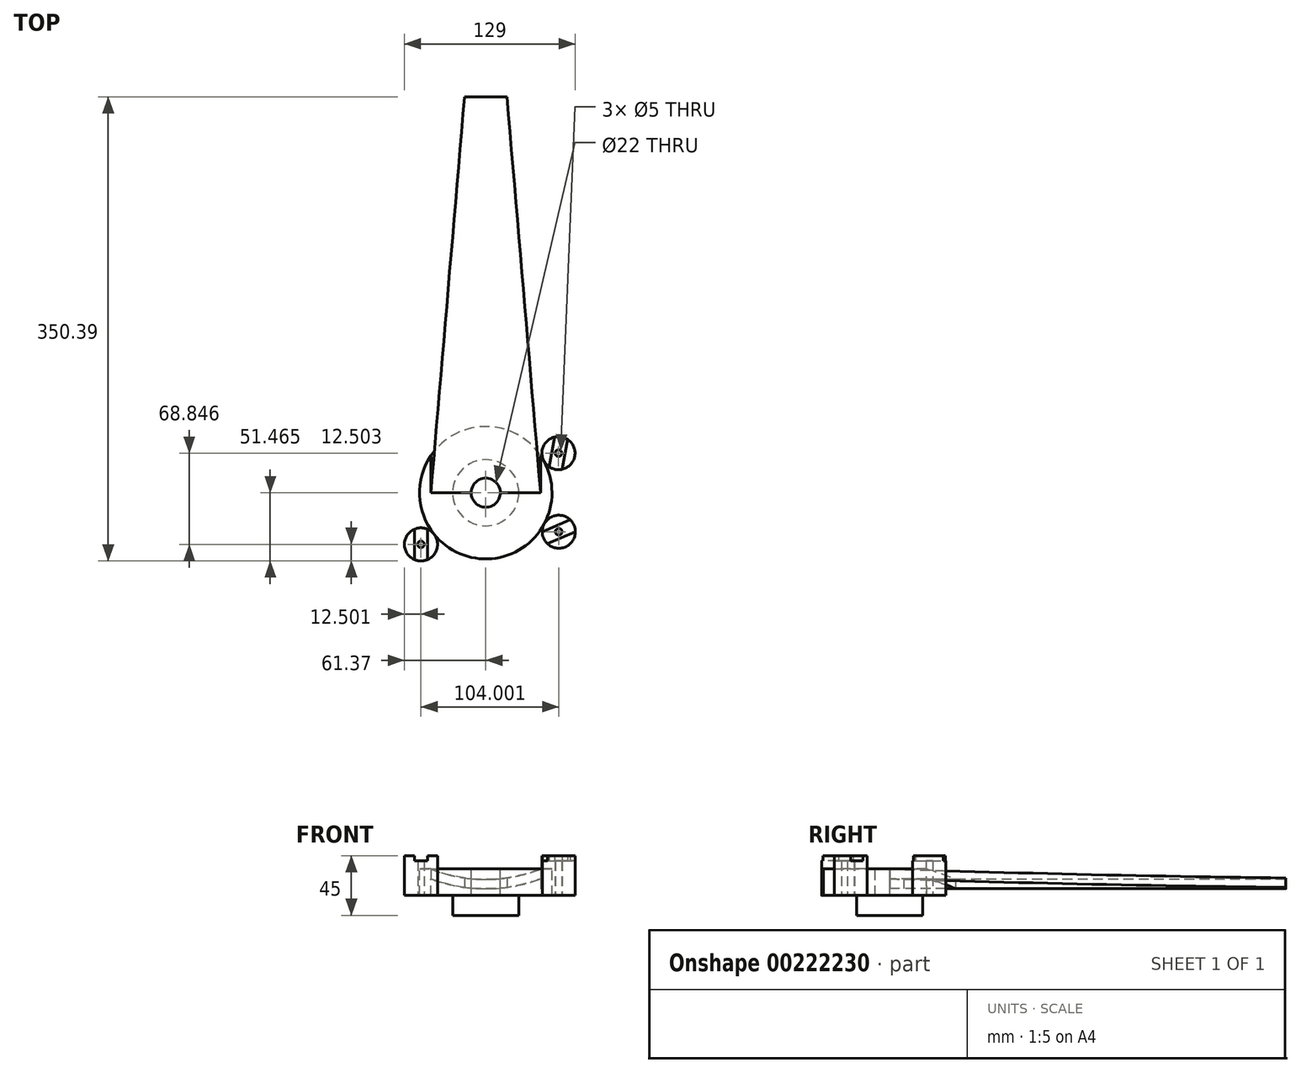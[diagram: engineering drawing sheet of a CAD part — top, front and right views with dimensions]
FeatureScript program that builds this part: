
annotation { "Feature Type Name" : "Feature", "Feature Type Description" : "" }
export const myFeature = defineFeature(function(context is Context, id is Id, definition is map)
    precondition{}
    {
        {
            var Q0;
            Q0=qCreatedBy(makeId("Top.planeOp"),FACE);
            var sketch = newSketch(context, id + "F0", { "sketchPlane" : qUnion([Q0])});
            skLineSegment(sketch, "E0", {"start": v(-16, 139.35) * mm, "end": v(-41.41, -159.57) * mm});
            skLineSegment(sketch, "E1", {"start": v(0, -151.5) * mm, "end": v(0, 130.37) * mm});
            skLineSegment(sketch, "E2.MirrorCS", {"start": v(16, 139.35) * mm, "end": v(41.41, -159.57) * mm});
            skLineSegment(sketch, "E3", {"start": v(-16, 139.35) * mm, "end": v(16, 139.35) * mm});
            skLineSegment(sketch, "E4", {"start": v(-41.41, -159.57) * mm, "end": v(41.41, -159.57) * mm});
            skSolve(sketch);
        }
        {
            var Q0;
            Q0=makeQuery(id+"F0.imprint","IMPRINT",FACE,{"disambiguationData":[TD([[makeQuery(id+"F0.imprint","IMPRINT",EDGE,{"derivedFrom":sQuery(id+"F0.wireOp",EDGE,"E0")}),1.0]])]});
            extrude(context, id + "F12", {"entities" : qUnion([Q0]), "depth" : 20 * mm});
        }
        {
            var Q0;
            Q0=makeQuery(id+"F12.opExtrude","CAP_FACE",FACE,{"disambiguationData":[OSD([sQuery(id+"F0.wireOp",EDGE,"E0"),sQuery(id+"F0.wireOp",EDGE,"E2.MirrorCS"),sQuery(id+"F0.wireOp",EDGE,"E3"),sQuery(id+"F0.wireOp",EDGE,"E4")])],"isStart":false});
            var sketch = newSketch(context, id + "F13", { "sketchPlane" : qUnion([Q0])});
            skCircle(sketch, "E5", {"center": v(0, -159.57) * mm, "radius": 50 * mm});
            skSolve(sketch);
        }
        {
            var Q0;
            {var subQ5=makeQuery(id+"F12.opExtrude","CAP_EDGE",EDGE,{"disambiguationData":[OSD([sQuery(id+"F0.wireOp",EDGE,"E4")])],"isStart":false});Q0=makeQuery(id+"F13.imprint","IMPRINT",FACE,{"disambiguationData":[TD([[makeQuery(id+"F13.imprint","IMPRINT",EDGE,{"derivedFrom":subQ5}),-1.0]])]});}
            var Q1;
            {var subQ5=makeQuery(id+"F12.opExtrude","CAP_EDGE",EDGE,{"disambiguationData":[OSD([sQuery(id+"F0.wireOp",EDGE,"E4")])],"isStart":false});Q1=makeQuery(id+"F13.imprint","IMPRINT",FACE,{"disambiguationData":[TD([[makeQuery(id+"F13.imprint","IMPRINT",EDGE,{"derivedFrom":subQ5}),1.0]])]});}
            extrude(context, id + "F1", {"entities" : qUnion([Q0, Q1]), "oppositeDirection" : true, "depth" : 20 * mm});
        }
        {
            var Q0;
            Q0=makeQuery(id+"F12.opExtrude","SWEPT_FACE",FACE,{"disambiguationData":[OSD([sQuery(id+"F0.wireOp",EDGE,"E4")])]});
            var sketch = newSketch(context, id + "F2", { "sketchPlane" : qUnion([Q0])});
            skArc(sketch, "E6", {"start": v(-41.41, 20) * mm, "mid": v(0, 12.05) * mm, "end": v(41.41, 20) * mm});
            skSolve(sketch);
        }
        {
            var Q0;
            Q0=makeQuery(id+"F2.imprint","IMPRINT",FACE,{"disambiguationData":[TD([[makeQuery(id+"F2.imprint","IMPRINT",EDGE,{"derivedFrom":sQuery(id+"F2.wireOp",EDGE,"E6")}),1.0]])]});
            extrude(context, id + "F14", {"entities" : qUnion([Q0]), "operationType" : NewBodyOperationType.REMOVE, "endBound" : BoundingType.THROUGH_ALL, "oppositeDirection" : true, "depth" : 25 * mm});
        }
        {
            var Q0;
            Q0=makeQuery(id+"F2.imprint","IMPRINT",FACE,{"disambiguationData":[TD([[makeQuery(id+"F2.imprint","IMPRINT",EDGE,{"derivedFrom":sQuery(id+"F2.wireOp",EDGE,"E6")}),-1.0]])]});
            var sketch = newSketch(context, id + "F3", { "sketchPlane" : qUnion([Q0])});
            skArc(sketch, "E7.0", {"start": v(-41.41, 20) * mm, "mid": v(0, 12.05) * mm, "end": v(41.41, 20) * mm});
            skArc(sketch, "E8.0", {"start": v(-44, 13.5) * mm, "mid": v(0, 5.05) * mm, "end": v(44, 13.5) * mm});
            skSolve(sketch);
        }
        {
            var Q0;
            Q0=makeQuery(id+"F2.imprint","IMPRINT",FACE,{"disambiguationData":[TD([[makeQuery(id+"F2.imprint","IMPRINT",EDGE,{"derivedFrom":sQuery(id+"F2.wireOp",EDGE,"E6")}),-1.0]])]});
            var sketch = newSketch(context, id + "F15", { "sketchPlane" : qUnion([Q0])});
            skLineSegment(sketch, "E9.0", {"start": v(-41.41, 20) * mm, "end": v(-41.41, 0) * mm});
            skLineSegment(sketch, "E10.0", {"start": v(-41.41, 0) * mm, "end": v(41.41, 0) * mm});
            skLineSegment(sketch, "E11.0", {"start": v(41.41, 20) * mm, "end": v(41.41, 0) * mm});
            skSolve(sketch);
        }
        {
            var Q0;
            Q0=qSketchRegion(id+"F15",true);
            var Q1;
            {var subQ1=sQuery(id+"F0.wireOp",EDGE,"E4");var subQ6=makeQuery(id+"F2.imprint","IMPRINT",EDGE,{"derivedFrom":makeQuery(id+"F12.opExtrude","CAP_EDGE",EDGE,{"disambiguationData":[OSD([subQ1])],"isStart":true})});Q1=makeQuery(id+"F3.imprint","IMPRINT",FACE,{"disambiguationData":[TD([[makeQuery(id+"F3.imprint","IMPRINT",EDGE,{"derivedFrom":subQ6}),1.0]])]});}
            extrude(context, id + "F4", {"entities" : qUnion([Q0, Q1]), "operationType" : NewBodyOperationType.REMOVE, "endBound" : BoundingType.THROUGH_ALL, "oppositeDirection" : true, "depth" : 25 * mm});
        }
        {
            var Q0;
            Q0=makeQuery(id+"F1.opExtrude","CAP_FACE",FACE,{"disambiguationData":[OSD([sQuery(id+"F13.wireOp",EDGE,"E5")])],"isStart":true});
            var sketch = newSketch(context, id + "F5", { "sketchPlane" : qUnion([Q0])});
            skCircle(sketch, "E12.0", {"center": v(0, -159.57) * mm, "radius": 50 * mm});
            skCircle(sketch, "E13", {"center": v(0, -159.57) * mm, "radius": 11 * mm});
            skSolve(sketch);
        }
        {
            var Q0;
            Q0=makeQuery(id+"F5.imprint","IMPRINT",FACE,{"disambiguationData":[TD([[makeQuery(id+"F5.imprint","IMPRINT",EDGE,{"derivedFrom":sQuery(id+"F5.wireOp",EDGE,"E13")}),1.0]])]});
            extrude(context, id + "F16", {"entities" : qUnion([Q0]), "operationType" : NewBodyOperationType.REMOVE, "endBound" : BoundingType.THROUGH_ALL, "oppositeDirection" : true, "depth" : 25 * mm});
        }
        {
            var Q0;
            Q0=makeQuery(id+"F1.opExtrude","CAP_FACE",FACE,{"disambiguationData":[OSD([sQuery(id+"F13.wireOp",EDGE,"E5")])],"isStart":true});
            var sketch = newSketch(context, id + "F6", { "sketchPlane" : qUnion([Q0])});
            skCircle(sketch, "E14.0", {"center": v(0, -159.57) * mm, "radius": 11 * mm});
            skSolve(sketch);
        }
        {
            var Q0;
            Q0=makeQuery(id+"F6.imprint","IMPRINT",FACE,{"disambiguationData":[TD([[makeQuery(id+"F6.imprint","IMPRINT",EDGE,{"derivedFrom":sQuery(id+"F6.wireOp",EDGE,"E14.0")}),1.0]])]});
            extrude(context, id + "F17", {"entities" : qUnion([Q0]), "operationType" : NewBodyOperationType.REMOVE, "endBound" : BoundingType.THROUGH_ALL, "oppositeDirection" : true, "depth" : 25 * mm});
        }
        {
            var Q0;
            Q0=makeQuery(id+"F1.opExtrude","CAP_FACE",FACE,{"disambiguationData":[OSD([sQuery(id+"F13.wireOp",EDGE,"E5")])],"isStart":false});
            var sketch = newSketch(context, id + "F18", { "sketchPlane" : qUnion([Q0])});
            skCircle(sketch, "E15", {"center": v(-48.87, 198.54) * mm, "radius": 12.5 * mm});
            skCircle(sketch, "E16", {"center": v(-48.87, 198.54) * mm, "radius": 2.5 * mm});
            skSolve(sketch);
        }
        {
            var Q0;
            Q0=makeQuery(id+"F18.imprint","IMPRINT",FACE,{"disambiguationData":[TD([[makeQuery(id+"F18.imprint","IMPRINT",EDGE,{"derivedFrom":sQuery(id+"F18.wireOp",EDGE,"E15")}),1.0]])]});
            extrude(context, id + "F7", {"entities" : qUnion([Q0]), "oppositeDirection" : true, "depth" : 30 * mm});
        }
        {
            var Q0;
            Q0=makeQuery(id+"F7.opExtrude","CAP_FACE",FACE,{"disambiguationData":[OSD([sQuery(id+"F18.wireOp",EDGE,"E15"),sQuery(id+"F18.wireOp",EDGE,"E16")])],"isStart":false});
            var sketch = newSketch(context, id + "F19", { "sketchPlane" : qUnion([Q0])});
            skLineSegment(sketch, "E17.bottom", {"start": v(-43.87, -180.65) * mm, "end": v(-53.87, -180.65) * mm});
            skLineSegment(sketch, "E17.top", {"start": v(-43.87, -212.63) * mm, "end": v(-53.87, -212.63) * mm});
            skLineSegment(sketch, "E17.left", {"start": v(-43.87, -180.65) * mm, "end": v(-43.87, -212.63) * mm});
            skLineSegment(sketch, "E17.right", {"start": v(-53.87, -180.65) * mm, "end": v(-53.87, -212.63) * mm});
            skCircle(sketch, "E18.0", {"center": v(-48.87, -198.54) * mm, "radius": 2.5 * mm});
            skSolve(sketch);
        }
        {
            var Q0;
            Q0=qSketchRegion(id+"F19",true);
            var Q1;
            Q1=makeQuery(id+"F19.imprint","IMPRINT",FACE,{"disambiguationData":[TD([[makeQuery(id+"F19.imprint","IMPRINT",EDGE,{"derivedFrom":sQuery(id+"F19.wireOp",EDGE,"E18.0")}),1.0]])]});
            extrude(context, id + "F8", {"entities" : qUnion([Q0, Q1]), "operationType" : NewBodyOperationType.REMOVE, "oppositeDirection" : true, "depth" : 4 * mm});
        }
        {
            var Q0;
            Q0=makeQuery(id+"F15.imprint","IMPRINT",FACE,{"disambiguationData":[TD([[makeQuery(id+"F15.imprint","IMPRINT",EDGE,{"derivedFrom":sQuery(id+"F15.wireOp",EDGE,"E9.0")}),1.0]])]});
            var sketch = newSketch(context, id + "F9", { "sketchPlane" : qUnion([Q0])});
            skLineSegment(sketch, "E19", {"start": v(0, 0) * mm, "end": v(0, 7.48) * mm});
            skSolve(sketch);
        }
        {
            var Q0;
            Q0=makeQuery(id+"F7.opExtrude","SWEPT_BODY",BODY,{"disambiguationData":[OSD([sQuery(id+"F18.wireOp",EDGE,"E15"),sQuery(id+"F18.wireOp",EDGE,"E16")])]});
            var Q1;
            Q1=sQuery(id+"F9.wireOp",EDGE,"E19");
            circularPattern(context, id + "F20", {"entities" : qUnion([Q0]), "axis" : qUnion([Q1]), "angle" : 170 * degree, "instanceCount" : 4, "equalSpace" : true});
        }
        {
            var Q0;
            Q0=makeQuery(id+"F20.opPattern","COPY",BODY,{"derivedFrom":makeQuery(id+"F7.opExtrude","SWEPT_BODY",BODY,{"disambiguationData":[OSD([sQuery(id+"F18.wireOp",EDGE,"E15"),sQuery(id+"F18.wireOp",EDGE,"E16")])]}),"instanceName":"1"});
            deleteBodies(context, id + "F10", {"entities" : qUnion([Q0])});
        }
        {
            var Q0;
            Q0=makeQuery(id+"F1.opExtrude","CAP_FACE",FACE,{"disambiguationData":[OSD([sQuery(id+"F13.wireOp",EDGE,"E5")])],"isStart":false});
            var sketch = newSketch(context, id + "F11", { "sketchPlane" : qUnion([Q0])});
            skLineSegment(sketch, "E20.0", {"start": v(-41.41, 159.57) * mm, "end": v(41.41, 159.57) * mm});
            skCircle(sketch, "E21.0", {"center": v(0, 159.57) * mm, "radius": 11 * mm});
            skCircle(sketch, "E22", {"center": v(0, 159.57) * mm, "radius": 25 * mm});
            skSolve(sketch);
        }
        {
            var Q0;
            Q0=qSketchRegion(id+"F11",true);
            var Q1;
            {var subQ0=sQuery(id+"F11.wireOp",EDGE,"E21.0");var subQ1=sQuery(id+"F11.wireOp",EDGE,"E20.0");var subQ2=makeQuery(id+"F11.imprint","INTERSECT",VERTEX,{"disambiguationData":[OD(0.0)],"derivedFrom":[subQ1,subQ0]});Q1=makeQuery(id+"F11.imprint","IMPRINT",FACE,{"disambiguationData":[TD([[makeQuery(id+"F11.imprint","IMPRINT",EDGE,{"disambiguationData":[TD([[subQ2,-1.0]])],"derivedFrom":subQ1}),-1.0]])]});}
            var Q2;
            {var subQ0=sQuery(id+"F11.wireOp",EDGE,"E21.0");var subQ1=sQuery(id+"F11.wireOp",EDGE,"E20.0");var subQ2=makeQuery(id+"F11.imprint","INTERSECT",VERTEX,{"disambiguationData":[OD(0.0)],"derivedFrom":[subQ1,subQ0]});Q2=makeQuery(id+"F11.imprint","IMPRINT",FACE,{"disambiguationData":[TD([[makeQuery(id+"F11.imprint","IMPRINT",EDGE,{"disambiguationData":[TD([[subQ2,-1.0]])],"derivedFrom":subQ1}),1.0]])]});}
            extrude(context, id + "F21", {"entities" : qUnion([Q0, Q1, Q2]), "depth" : 15 * mm});
        }
    });
